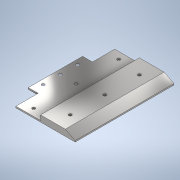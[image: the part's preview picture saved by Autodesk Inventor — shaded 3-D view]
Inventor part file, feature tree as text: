
AUTODESK INVENTOR PART (.ipt)
format: ipt  version: 2021 (Build 250183000, 183)  size: 178,688 bytes
history: native  units: mm
features: sketch x5, other x3, extrude x3, hole x2, chamfer x1
ambient origin geometry x8: Origin, YZ Plane, XZ Plane, XY Plane, X Axis, Y Axis, Z Axis, Center Point
bodies: Body1 (feature_tree)
feature tree (14):
  other  "Sólido1"
  extrude  "Extrusão1"  Depth=100.0mm
  extrude  "Extrusão2"  Depth=25.0mm
  extrude  "Extrusão3"  Depth=1.5mm
  hole  "Furo3"  [1 undecoded]
  chamfer  "Chanfro1"  [1 undecoded]
  hole  "Furo4"  [1 undecoded]
  sketch  "Esboço1"  dims[d0=70.0mm d1=100.0mm]
  sketch  "Esboço2"  dims[d2=6.35mm d3=0.0mm d7=25.0mm]
  other  "Contorno projetado1"
  sketch  "Esboço3"  dims[d8=4.633849mm d9=1.5mm]
  other  "Contorno projetado2"
  sketch  "Esboço10"  dims[d10=0.0mm d11=0.0mm d12=10.0mm]
  sketch  "Esboço11"  dims[d13=55.0mm d14=0.0mm d15=0.0mm d16=35.0mm d61=10.0mm d62=10.0mm d63=50.0mm d64=5.0mm d65=3.0mm d66=6.0mm d67=4.0mm d68=2.0mm d69=90.0deg d70=8.0mm d71=20.594885mm d72=1.5mm d73=2.0mm d74=45.0deg d75=10.0mm d76=35.0mm d77=35.0mm d78=29.0mm d79=43.0mm d80=43.0mm d81=3.0mm d82=6.0mm d83=4.0mm d84=2.0mm d85=90.0deg d86=8.0mm d87=20.594885mm]
note: 3 required parameter values undecoded (feature->parameter linkage not recoverable at this tier; creation-order binding heuristic only, values carry confidence <= 0.55)
